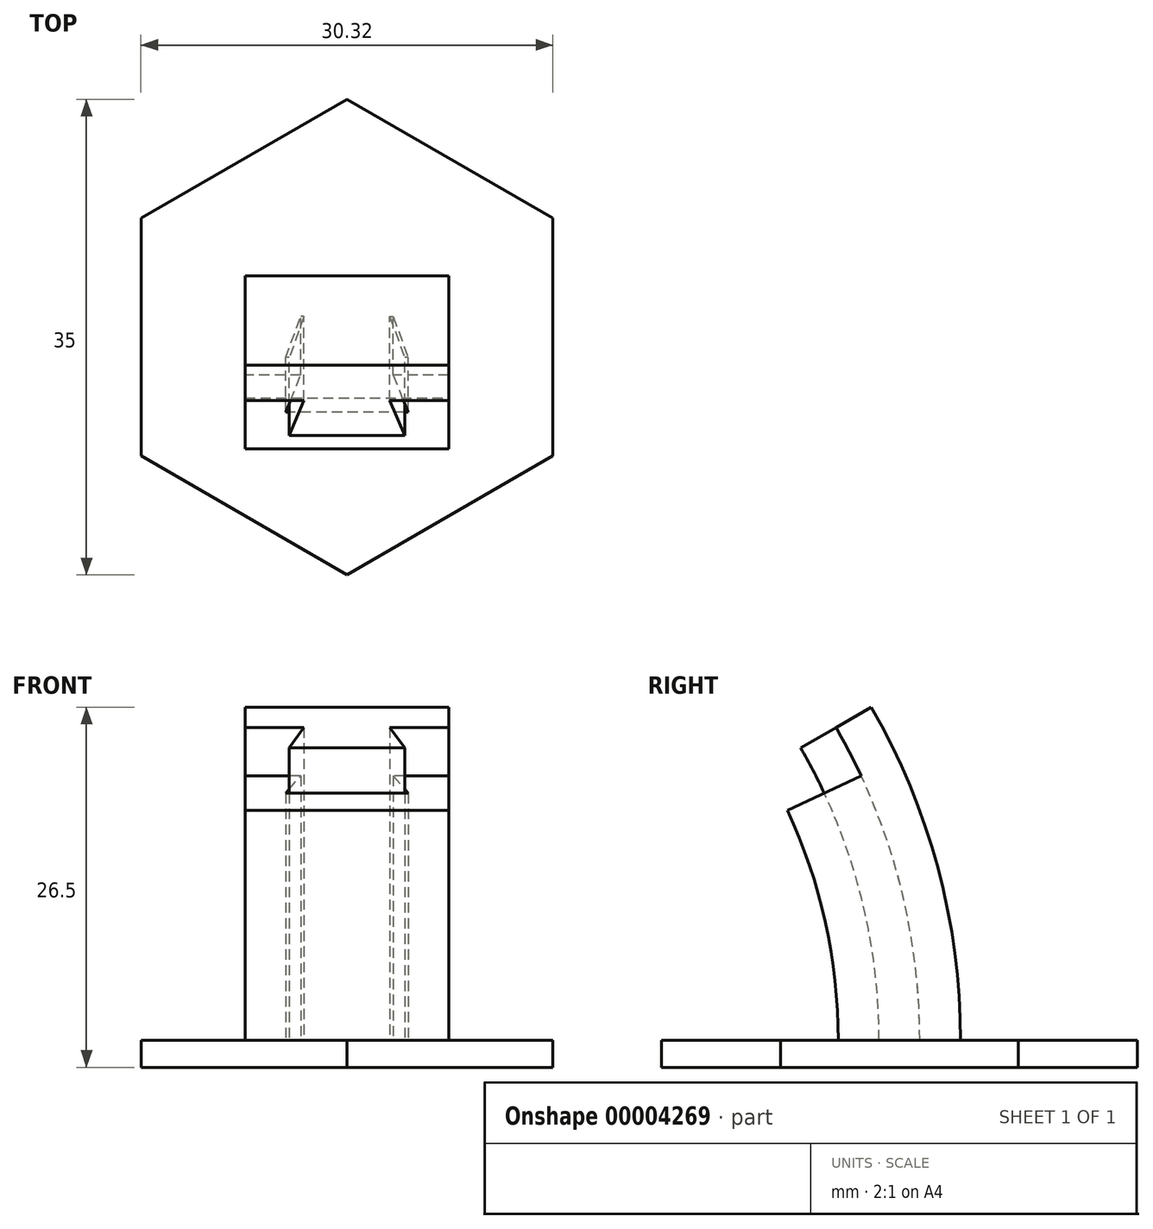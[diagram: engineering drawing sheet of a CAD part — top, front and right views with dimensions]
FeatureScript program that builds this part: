
annotation { "Feature Type Name" : "Feature", "Feature Type Description" : "" }
export const myFeature = defineFeature(function(context is Context, id is Id, definition is map)
    precondition{}
    {
        {
            var Q0;
            Q0=qCreatedBy(makeId("Top.planeOp"),FACE);
            var sketch = newSketch(context, id + "F0", { "sketchPlane" : qUnion([Q0])});
            skPoint(sketch, "E0", {"position": v(0, 0) * mm});
            skLineSegment(sketch, "E1", {"start": v(-7.5, 0) * mm, "end": v(7.5, 0) * mm});
            skLineSegment(sketch, "E2", {"start": v(7.5, 0) * mm, "end": v(7.5, 6) * mm});
            skLineSegment(sketch, "E3", {"start": v(7.5, 6) * mm, "end": v(3.4, 6) * mm});
            skLineSegment(sketch, "E4", {"start": v(3.4, 6) * mm, "end": v(4.5, 3) * mm});
            skLineSegment(sketch, "E5", {"start": v(4.5, 3) * mm, "end": v(-4.5, 3) * mm});
            skLineSegment(sketch, "E6", {"start": v(-4.5, 3) * mm, "end": v(-3.4, 6) * mm});
            skLineSegment(sketch, "E7", {"start": v(-3.4, 6) * mm, "end": v(-7.5, 6) * mm});
            skLineSegment(sketch, "E8", {"start": v(-7.5, 6) * mm, "end": v(-7.5, 3) * mm});
            skPoint(sketch, "E9", {"position": v(-7.5, 3) * mm});
            skLineSegment(sketch, "E10", {"start": v(-7.5, 3) * mm, "end": v(-4.5, 3) * mm, "construction": true});
            skLineSegment(sketch, "E11", {"start": v(-7.5, 3) * mm, "end": v(-7.5, 0) * mm});
            skLineSegment(sketch, "E12", {"start": v(-7.5, 6) * mm, "end": v(-7.5, 9) * mm});
            skLineSegment(sketch, "E13", {"start": v(-7.5, 9) * mm, "end": v(7.5, 9) * mm});
            skLineSegment(sketch, "E14", {"start": v(7.5, 9) * mm, "end": v(7.5, 6) * mm});
            skLineSegment(sketch, "E15", {"start": v(-7.5, -40) * mm, "end": v(7.5, -40) * mm, "construction": true});
            skLineSegment(sketch, "E16", {"start": v(0, 9) * mm, "end": v(0, 0) * mm, "construction": true});
            skCircle(sketch, "E17.cCircle", {"center": v(0, 4.5) * mm, "radius": 17.5 * mm, "construction": true});
            skLineSegment(sketch, "E17.0", {"start": v(15.16, -4.25) * mm, "end": v(0, -13) * mm});
            skLineSegment(sketch, "E17.1", {"start": v(0, -13) * mm, "end": v(-15.16, -4.25) * mm});
            skLineSegment(sketch, "E17.2", {"start": v(-15.16, -4.25) * mm, "end": v(-15.16, 13.25) * mm});
            skLineSegment(sketch, "E17.3", {"start": v(-15.16, 13.25) * mm, "end": v(0, 22) * mm});
            skLineSegment(sketch, "E17.4", {"start": v(0, 22) * mm, "end": v(15.16, 13.25) * mm});
            skLineSegment(sketch, "E17.5", {"start": v(15.16, 13.25) * mm, "end": v(15.16, -4.25) * mm});
            skLineSegment(sketch, "E18", {"start": v(-3.16, 6) * mm, "end": v(-4.25, 3) * mm});
            skLineSegment(sketch, "E19", {"start": v(3.16, 6) * mm, "end": v(4.25, 3) * mm});
            skLineSegment(sketch, "E20", {"start": v(-3.4, 6) * mm, "end": v(-3.16, 6) * mm});
            skLineSegment(sketch, "E21", {"start": v(3.16, 6) * mm, "end": v(3.4, 6) * mm});
            skSolve(sketch);
        }
        {
            var Q0;
            Q0=makeQuery(id+"F0.imprint","IMPRINT",FACE,{"disambiguationData":[TD([[makeQuery(id+"F0.imprint","IMPRINT",EDGE,{"derivedFrom":sQuery(id+"F0.wireOp",EDGE,"E1")}),1.0]])]});
            var Q1;
            Q1=sQuery(id+"F0.wireOp",EDGE,"E15");
            revolve(context, id + "F1", {"entities" : qUnion([Q0]), "axis" : qUnion([Q1]), "revolveType" : RevolveType.ONE_DIRECTION, "angle" : 25 * degree});
        }
        {
            var Q0;
            Q0=makeQuery(id+"F0.imprint","IMPRINT",FACE,{"disambiguationData":[TD([[makeQuery(id+"F0.imprint","IMPRINT",EDGE,{"derivedFrom":sQuery(id+"F0.wireOp",EDGE,"E3")}),-1.0]])]});
            var Q1;
            Q1=sQuery(id+"F0.wireOp",EDGE,"E15");
            revolve(context, id + "F2", {"entities" : qUnion([Q0]), "axis" : qUnion([Q1]), "revolveType" : RevolveType.ONE_DIRECTION, "angle" : 30 * degree});
        }
        {
            var Q0;
            Q0=makeQuery(id+"F0.imprint","IMPRINT",FACE,{"disambiguationData":[TD([[makeQuery(id+"F0.imprint","IMPRINT",EDGE,{"derivedFrom":sQuery(id+"F0.wireOp",EDGE,"E1")}),-1.0]])]});
            var Q1;
            Q1=makeQuery(id+"F0.imprint","IMPRINT",FACE,{"disambiguationData":[TD([[makeQuery(id+"F0.imprint","IMPRINT",EDGE,{"derivedFrom":sQuery(id+"F0.wireOp",EDGE,"E3")}),-1.0]])]});
            var Q2;
            Q2=makeQuery(id+"F0.imprint","IMPRINT",FACE,{"disambiguationData":[TD([[makeQuery(id+"F0.imprint","IMPRINT",EDGE,{"derivedFrom":sQuery(id+"F0.wireOp",EDGE,"E1")}),1.0]])]});
            var Q3;
            {var subQ1=sQuery(id+"F0.wireOp",EDGE,"E6");Q3=makeQuery(id+"F0.imprint","IMPRINT",FACE,{"disambiguationData":[TD([[makeQuery(id+"F0.imprint","IMPRINT",EDGE,{"derivedFrom":subQ1}),-1.0]])]});}
            var Q4;
            {var subQ2=sQuery(id+"F0.wireOp",EDGE,"E4");Q4=makeQuery(id+"F0.imprint","IMPRINT",FACE,{"disambiguationData":[TD([[makeQuery(id+"F0.imprint","IMPRINT",EDGE,{"derivedFrom":subQ2}),-1.0]])]});}
            extrude(context, id + "F3", {"entities" : qUnion([Q0, Q1, Q2, Q3, Q4]), "operationType" : NewBodyOperationType.ADD, "oppositeDirection" : true, "depth" : 2 * mm});
        }
    });
